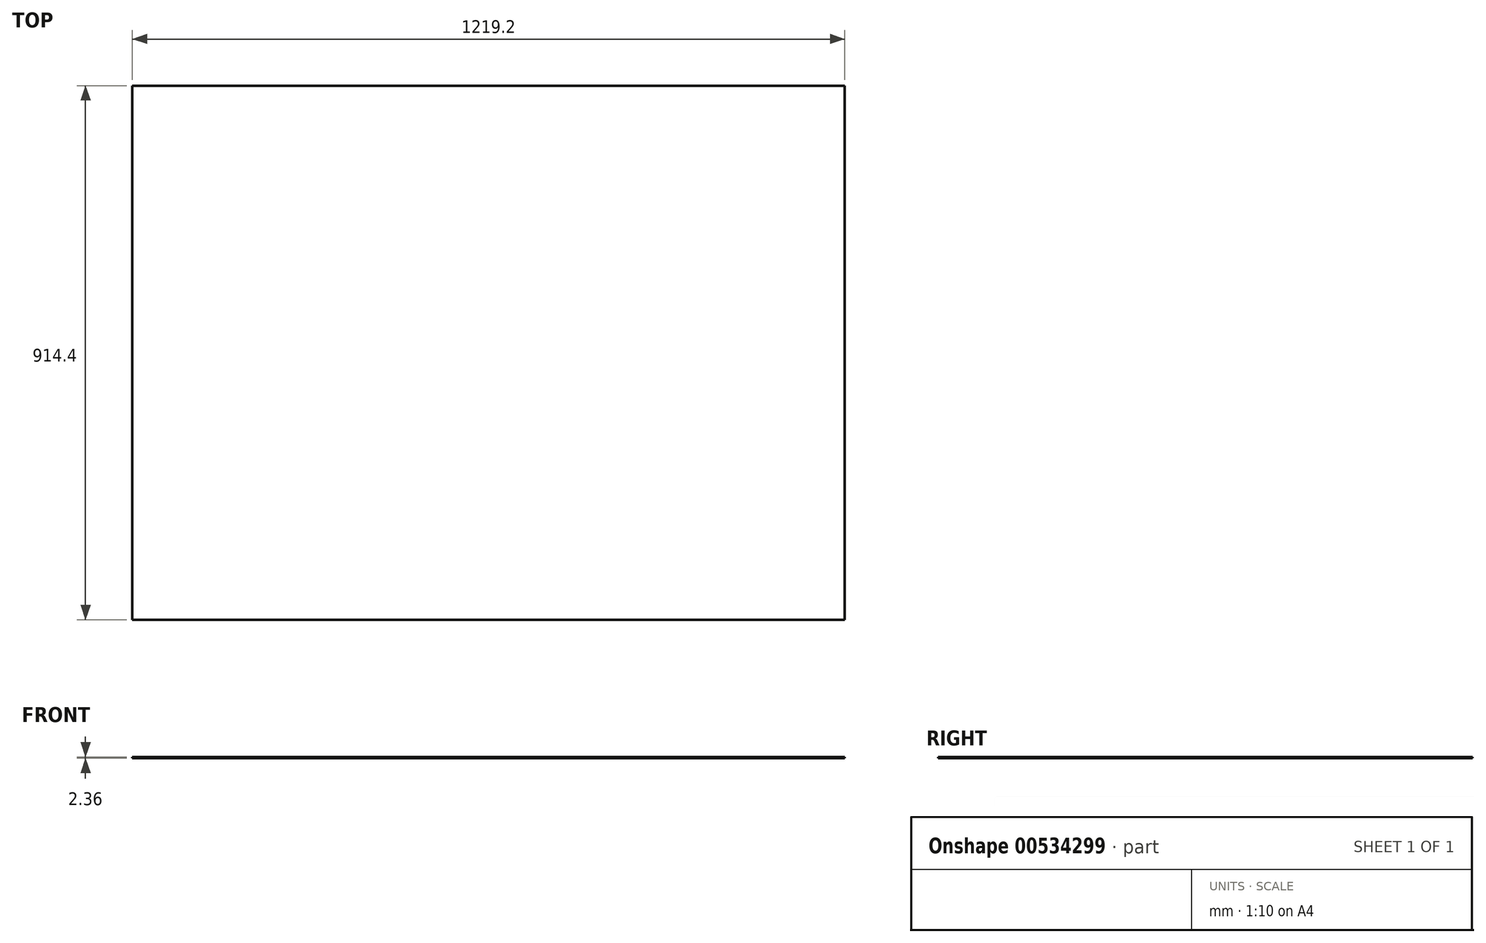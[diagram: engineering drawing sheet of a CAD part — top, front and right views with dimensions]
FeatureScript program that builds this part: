
annotation { "Feature Type Name" : "Feature", "Feature Type Description" : "" }
export const myFeature = defineFeature(function(context is Context, id is Id, definition is map)
    precondition{}
    {
        {
            var Q0;
            Q0=qCreatedBy(makeId("Top.planeOp"),FACE);
            var sketch = newSketch(context, id + "F0", { "sketchPlane" : qUnion([Q0])});
            skLineSegment(sketch, "E0.bottom", {"start": v(609.6, -457.2) * mm, "end": v(-609.6, -457.2) * mm});
            skLineSegment(sketch, "E0.top", {"start": v(609.6, 457.2) * mm, "end": v(-609.6, 457.2) * mm});
            skLineSegment(sketch, "E0.left", {"start": v(609.6, -457.2) * mm, "end": v(609.6, 457.2) * mm});
            skLineSegment(sketch, "E0.right", {"start": v(-609.6, -457.2) * mm, "end": v(-609.6, 457.2) * mm});
            skPoint(sketch, "E0.middle", {"position": v(0, 0) * mm});
            skSolve(sketch);
        }
        {
            var Q0;
            Q0 = qSketchRegion(id + "F0", true);
            extrude(context, id + "F1", {"entities" : qUnion([Q0]), "depth" : 2.36 * mm, "offsetDistance" : 25.4 * mm});
        }
    });
